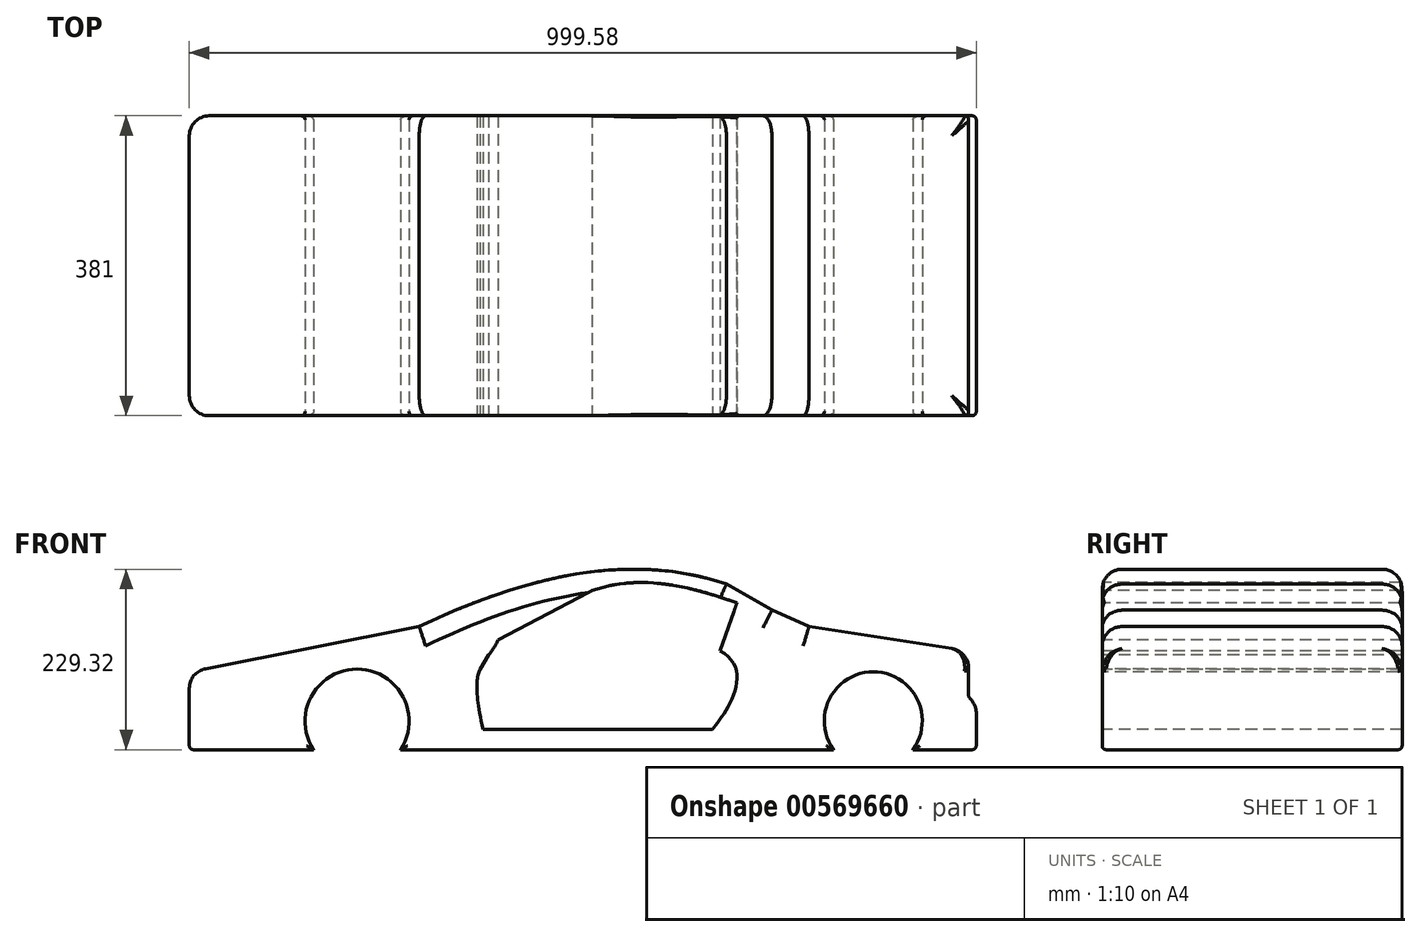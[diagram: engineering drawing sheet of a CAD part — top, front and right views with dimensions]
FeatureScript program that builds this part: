
annotation { "Feature Type Name" : "Feature", "Feature Type Description" : "" }
export const myFeature = defineFeature(function(context is Context, id is Id, definition is map)
    precondition{}
    {
        {
            var Q0;
            Q0=qCreatedBy(makeId("Front.planeOp"),FACE);
            var sketch = newSketch(context, id + "F0", { "sketchPlane" : qUnion([Q0])});
            skLineSegment(sketch, "E0", {"start": v(-159.83, 15.52) * mm, "end": v(-40.62, 78.35) * mm});
            skLineSegment(sketch, "E1", {"start": v(143.58, 62.75) * mm, "end": v(121.86, 1.9) * mm});
            skFitSpline(sketch, "E2", {"points": [v(121.86, 1.9) * mm, v(112.4, -97.7) * mm], "startDerivative": vector(144.95, -75.54) * mm, "endDerivative": vector(-38.97, -46.14) * mm});
            skPoint(sketch, "E3.end.orphan", {"position": v(112.4, -98.09) * mm});
            skLineSegment(sketch, "E4", {"start": v(-179.07, -97.77) * mm, "end": v(112.4, -97.7) * mm});
            skFitSpline(sketch, "E5", {"points": [v(-40.62, 78.35) * mm, v(143.58, 62.75) * mm], "startDerivative": vector(200.14, 72.05) * mm, "endDerivative": vector(136.97, -48.45) * mm});
            skFitSpline(sketch, "E6", {"points": [v(-159.83, 15.52) * mm, v(-179.07, -97.77) * mm], "startDerivative": vector(-50.7, -105.63) * mm, "endDerivative": vector(57.75, -262.4) * mm});
            skLineSegment(sketch, "E7", {"start": v(-183, -21.52) * mm, "end": v(-159.83, 15.52) * mm});
            skLineSegment(sketch, "E8", {"start": v(-141.05, 6.6) * mm, "end": v(-24.61, 69.5) * mm});
            skLineSegment(sketch, "E9", {"start": v(120.46, 51.67) * mm, "end": v(102.6, 6.6) * mm});
            skLineSegment(sketch, "E10", {"start": v(102.6, 6.6) * mm, "end": v(-141.05, 6.6) * mm});
            skFitSpline(sketch, "E11", {"points": [v(-24.61, 69.5) * mm, v(120.46, 51.67) * mm], "startDerivative": vector(146.48, 42.25) * mm, "endDerivative": vector(121.13, -81.7) * mm});
            skSolve(sketch);
        }
        {
            var Q0;
            Q0=qCreatedBy(makeId("Front.planeOp"),FACE);
            var sketch = newSketch(context, id + "F1", { "sketchPlane" : qUnion([Q0])});
            skLineSegment(sketch, "E12", {"start": v(-552.05, -123.74) * mm, "end": v(-394.25, -123.74) * mm});
            skLineSegment(sketch, "E13", {"start": v(447.53, -123.74) * mm, "end": v(447.53, -61.87) * mm});
            skArc(sketch, "E14", {"start": v(-283.72, -123.74) * mm, "mid": v(-338.99, -21.37) * mm, "end": v(-394.25, -123.74) * mm});
            skArc(sketch, "E15", {"start": v(367.16, -123.74) * mm, "mid": v(316.8, -24.83) * mm, "end": v(266.43, -123.74) * mm});
            skLineSegment(sketch, "E16", {"start": v(130.19, 86.59) * mm, "end": v(188.02, 53.54) * mm});
            skLineSegment(sketch, "E17", {"start": v(188.02, 53.54) * mm, "end": v(235, 32.73) * mm});
            skLineSegment(sketch, "E18", {"start": v(235, 32.73) * mm, "end": v(437.91, 1.48) * mm});
            skPoint(sketch, "E19.end.orphan", {"position": v(-552.05, 0) * mm});
            skPoint(sketch, "E20.start.orphan", {"position": v(-774.93, 63.25) * mm});
            skFitSpline(sketch, "E21", {"points": [v(-259.98, 32.73) * mm, v(130.19, 86.59) * mm], "startDerivative": vector(431.12, 205.17) * mm, "endDerivative": vector(351.11, -119.8) * mm});
            skLineSegment(sketch, "E22.trimOffspring", {"start": v(-283.72, -123.74) * mm, "end": v(266.43, -123.74) * mm});
            skLineSegment(sketch, "E23.trimOffspring", {"start": v(367.16, -123.74) * mm, "end": v(447.53, -123.74) * mm});
            skPoint(sketch, "E24", {"position": v(-593.79, -61.87) * mm});
            skLineSegment(sketch, "E25", {"start": v(437.91, 1.48) * mm, "end": v(437.91, -57.1) * mm});
            skLineSegment(sketch, "E26", {"start": v(437.91, -57.1) * mm, "end": v(447.53, -61.87) * mm});
            skPoint(sketch, "E27.orphan", {"position": v(447.53, 0) * mm});
            skPoint(sketch, "E28.0.internal.orphan", {"position": v(-663.5, -30.24) * mm});
            skPoint(sketch, "E28.endDerivative.orphan", {"position": v(-665.87, -61.87) * mm});
            skPoint(sketch, "E29.orphan", {"position": v(-490.33, 0) * mm});
            skPoint(sketch, "E30.trimOffspring.startDerivative.orphan", {"position": v(-791.85, 0) * mm});
            skPoint(sketch, "E31.start.orphan", {"position": v(-697.24, -123.74) * mm});
            skLineSegment(sketch, "E32", {"start": v(-552.05, -123.74) * mm, "end": v(-552.05, -24.93) * mm});
            skLineSegment(sketch, "E33", {"start": v(-552.05, -24.93) * mm, "end": v(-259.98, 32.73) * mm});
            skSolve(sketch);
        }
        {
            var Q0;
            Q0=makeQuery(id+"F1.imprint","IMPRINT",FACE,{"disambiguationData":[TD([[makeQuery(id+"F1.imprint","IMPRINT",EDGE,{"derivedFrom":sQuery(id+"F1.wireOp",EDGE,"E12")}),1.0]])]});
            extrude(context, id + "F2", {"entities" : qUnion([Q0]), "oppositeDirection" : true, "depth" : 381 * mm, "offsetDistance" : 25.4 * mm});
        }
        {
            var Q0;
            Q0=makeQuery(id+"F0.imprint","IMPRINT",FACE,{"disambiguationData":[TD([[makeQuery(id+"F0.imprint","IMPRINT",EDGE,{"derivedFrom":sQuery(id+"F0.wireOp",EDGE,"E0")}),-1.0]])]});
            extrude(context, id + "F3", {"entities" : qUnion([Q0]), "operationType" : NewBodyOperationType.REMOVE, "oppositeDirection" : true, "depth" : 381 * mm, "offsetDistance" : 25.4 * mm});
        }
        {
            var Q0;
            Q0=makeQuery(id+"F3.boolean.opBoolean","SPLIT",FACE,{"disambiguationData":[TD([makeQuery(id+"F3.opExtrude","SWEPT_FACE",FACE,{"disambiguationData":[OSD([sQuery(id+"F0.wireOp",EDGE,"E8")])]})])],"derivedFrom":makeQuery(id+"F2.opExtrude","CAP_FACE",FACE,{"disambiguationData":[OSD([sQuery(id+"F1.wireOp",EDGE,"E12"),sQuery(id+"F1.wireOp",EDGE,"E13"),sQuery(id+"F1.wireOp",EDGE,"E14"),sQuery(id+"F1.wireOp",EDGE,"E15"),sQuery(id+"F1.wireOp",EDGE,"E16"),sQuery(id+"F1.wireOp",EDGE,"E17"),sQuery(id+"F1.wireOp",EDGE,"E18"),sQuery(id+"F1.wireOp",EDGE,"E21"),sQuery(id+"F1.wireOp",EDGE,"E22.trimOffspring"),sQuery(id+"F1.wireOp",EDGE,"E23.trimOffspring"),sQuery(id+"F1.wireOp",EDGE,"E25"),sQuery(id+"F1.wireOp",EDGE,"E26"),sQuery(id+"F1.wireOp",EDGE,"E32"),sQuery(id+"F1.wireOp",EDGE,"E33")])],"isStart":true})});
            extrude(context, id + "F4", {"entities" : qUnion([Q0]), "operationType" : NewBodyOperationType.REMOVE, "oppositeDirection" : true, "depth" : 381 * mm, "offsetDistance" : 25.4 * mm});
        }
        {
            var Q0;
            Q0=makeQuery(id+"F2.opExtrude","CAP_EDGE",EDGE,{"disambiguationData":[OSD([sQuery(id+"F1.wireOp",EDGE,"E18")])],"isStart":true});
            var Q1;
            Q1=makeQuery(id+"F2.opExtrude","CAP_EDGE",EDGE,{"disambiguationData":[OSD([sQuery(id+"F1.wireOp",EDGE,"E16")])],"isStart":true});
            var Q2;
            Q2=makeQuery(id+"F2.opExtrude","CAP_EDGE",EDGE,{"disambiguationData":[OSD([sQuery(id+"F1.wireOp",EDGE,"E17")])],"isStart":true});
            var Q3;
            Q3=makeQuery(id+"F2.opExtrude","CAP_EDGE",EDGE,{"disambiguationData":[OSD([sQuery(id+"F1.wireOp",EDGE,"E21")])],"isStart":true});
            var Q4;
            Q4=makeQuery(id+"F2.opExtrude","CAP_EDGE",EDGE,{"disambiguationData":[OSD([sQuery(id+"F1.wireOp",EDGE,"E33")])],"isStart":true});
            var Q5;
            Q5=makeQuery(id+"F2.opExtrude","CAP_EDGE",EDGE,{"disambiguationData":[OSD([sQuery(id+"F1.wireOp",EDGE,"E32")])],"isStart":true});
            var Q6;
            Q6=makeQuery(id+"F2.opExtrude","SWEPT_EDGE",EDGE,{"disambiguationData":[OSD([sQuery(id+"F1.wireOp",EDGE,"E32"),sQuery(id+"F1.wireOp",EDGE,"E33")])]});
            var Q7;
            Q7=makeQuery(id+"F2.opExtrude","CAP_EDGE",EDGE,{"disambiguationData":[OSD([sQuery(id+"F1.wireOp",EDGE,"E32")])],"isStart":false});
            var Q8;
            Q8=makeQuery(id+"F2.opExtrude","CAP_EDGE",EDGE,{"disambiguationData":[OSD([sQuery(id+"F1.wireOp",EDGE,"E33")])],"isStart":false});
            var Q9;
            Q9=makeQuery(id+"F2.opExtrude","CAP_EDGE",EDGE,{"disambiguationData":[OSD([sQuery(id+"F1.wireOp",EDGE,"E21")])],"isStart":false});
            var Q10;
            Q10=makeQuery(id+"F2.opExtrude","CAP_EDGE",EDGE,{"disambiguationData":[OSD([sQuery(id+"F1.wireOp",EDGE,"E16")])],"isStart":false});
            var Q11;
            Q11=makeQuery(id+"F2.opExtrude","CAP_EDGE",EDGE,{"disambiguationData":[OSD([sQuery(id+"F1.wireOp",EDGE,"E17")])],"isStart":false});
            var Q12;
            Q12=makeQuery(id+"F2.opExtrude","CAP_EDGE",EDGE,{"disambiguationData":[OSD([sQuery(id+"F1.wireOp",EDGE,"E18")])],"isStart":false});
            var Q13;
            Q13=makeQuery(id+"F2.opExtrude","SWEPT_EDGE",EDGE,{"disambiguationData":[OSD([sQuery(id+"F1.wireOp",EDGE,"E18"),sQuery(id+"F1.wireOp",EDGE,"E25")])]});
            var Q14;
            Q14=makeQuery(id+"F2.opExtrude","SWEPT_EDGE",EDGE,{"disambiguationData":[OSD([sQuery(id+"F1.wireOp",EDGE,"E13"),sQuery(id+"F1.wireOp",EDGE,"E26")])]});
            fillet(context, id + "F5", {"entities" : qUnion([Q0, Q1, Q2, Q3, Q4, Q5, Q6, Q7, Q8, Q9, Q10, Q11, Q12, Q13, Q14]), "radius" : 25.4 * mm, "tangentPropagation" : true, "allowEdgeOverflow" : false});
        }
        {
            var Q0;
            Q0=makeQuery(id+"F2.opExtrude","CAP_EDGE",EDGE,{"disambiguationData":[OSD([sQuery(id+"F1.wireOp",EDGE,"E25")])],"isStart":false});
            var Q1;
            Q1=makeQuery(id+"F2.opExtrude","CAP_EDGE",EDGE,{"disambiguationData":[OSD([sQuery(id+"F1.wireOp",EDGE,"E13")])],"isStart":false});
            var Q2;
            Q2=makeQuery(id+"F2.opExtrude","CAP_EDGE",EDGE,{"disambiguationData":[OSD([sQuery(id+"F1.wireOp",EDGE,"E23.trimOffspring")])],"isStart":false});
            var Q3;
            Q3=makeQuery(id+"F2.opExtrude","CAP_EDGE",EDGE,{"disambiguationData":[OSD([sQuery(id+"F1.wireOp",EDGE,"E15")])],"isStart":false});
            var Q4;
            Q4=makeQuery(id+"F2.opExtrude","CAP_EDGE",EDGE,{"disambiguationData":[OSD([sQuery(id+"F1.wireOp",EDGE,"E22.trimOffspring")])],"isStart":false});
            var Q5;
            Q5=makeQuery(id+"F2.opExtrude","CAP_EDGE",EDGE,{"disambiguationData":[OSD([sQuery(id+"F1.wireOp",EDGE,"E14")])],"isStart":false});
            var Q6;
            Q6=makeQuery(id+"F2.opExtrude","CAP_EDGE",EDGE,{"disambiguationData":[OSD([sQuery(id+"F1.wireOp",EDGE,"E12")])],"isStart":false});
            var Q7;
            Q7=makeQuery(id+"F2.opExtrude","SWEPT_EDGE",EDGE,{"disambiguationData":[OSD([sQuery(id+"F1.wireOp",EDGE,"E12"),sQuery(id+"F1.wireOp",EDGE,"E32")])]});
            var Q8;
            Q8=makeQuery(id+"F2.opExtrude","CAP_EDGE",EDGE,{"disambiguationData":[OSD([sQuery(id+"F1.wireOp",EDGE,"E12")])],"isStart":true});
            var Q9;
            Q9=makeQuery(id+"F2.opExtrude","CAP_EDGE",EDGE,{"disambiguationData":[OSD([sQuery(id+"F1.wireOp",EDGE,"E14")])],"isStart":true});
            var Q10;
            Q10=makeQuery(id+"F2.opExtrude","CAP_EDGE",EDGE,{"disambiguationData":[OSD([sQuery(id+"F1.wireOp",EDGE,"E22.trimOffspring")])],"isStart":true});
            var Q11;
            Q11=makeQuery(id+"F2.opExtrude","CAP_EDGE",EDGE,{"disambiguationData":[OSD([sQuery(id+"F1.wireOp",EDGE,"E15")])],"isStart":true});
            var Q12;
            Q12=makeQuery(id+"F2.opExtrude","CAP_EDGE",EDGE,{"disambiguationData":[OSD([sQuery(id+"F1.wireOp",EDGE,"E23.trimOffspring")])],"isStart":true});
            var Q13;
            Q13=makeQuery(id+"F2.opExtrude","CAP_EDGE",EDGE,{"disambiguationData":[OSD([sQuery(id+"F1.wireOp",EDGE,"E25")])],"isStart":true});
            var Q14;
            Q14=makeQuery(id+"F2.opExtrude","CAP_EDGE",EDGE,{"disambiguationData":[OSD([sQuery(id+"F1.wireOp",EDGE,"E13")])],"isStart":true});
            var Q15;
            Q15=makeQuery(id+"F5.opFillet","BLEND_EDGE",EDGE,{"blendedFrom":[makeQuery(id+"F2.opExtrude","SWEPT_EDGE",EDGE,{"disambiguationData":[OSD([sQuery(id+"F1.wireOp",EDGE,"E13"),sQuery(id+"F1.wireOp",EDGE,"E26")])]}),makeQuery(id+"F2.opExtrude","SWEPT_FACE",FACE,{"disambiguationData":[OSD([sQuery(id+"F1.wireOp",EDGE,"E25")])]})],"blendedInto":[makeQuery(id+"F2.opExtrude","SWEPT_FACE",FACE,{"disambiguationData":[OSD([sQuery(id+"F1.wireOp",EDGE,"E25")])]})]});
            var Q16;
            Q16=makeQuery(id+"F2.opExtrude","SWEPT_EDGE",EDGE,{"disambiguationData":[OSD([sQuery(id+"F1.wireOp",EDGE,"E13"),sQuery(id+"F1.wireOp",EDGE,"E23.trimOffspring")])]});
            fillet(context, id + "F6", {"entities" : qUnion([Q0, Q1, Q2, Q3, Q4, Q5, Q6, Q7, Q8, Q9, Q10, Q11, Q12, Q13, Q14, Q15, Q16]), "radius" : 5.08 * mm, "tangentPropagation" : true, "allowEdgeOverflow" : false});
        }
    });
